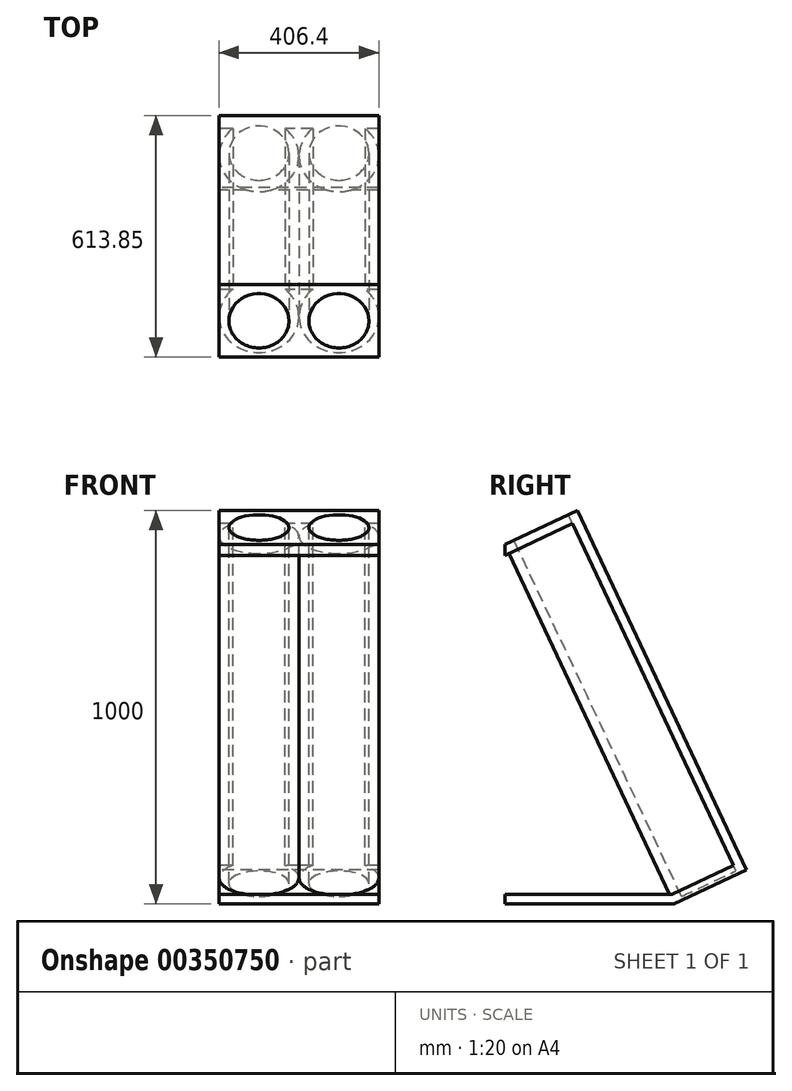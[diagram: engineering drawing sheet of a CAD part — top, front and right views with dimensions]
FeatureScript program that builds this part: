
annotation { "Feature Type Name" : "Feature", "Feature Type Description" : "" }
export const myFeature = defineFeature(function(context is Context, id is Id, definition is map)
    precondition{}
    {
        {
            var Q0;
            Q0=qCreatedBy(makeId("Right.planeOp"),FACE);
            var sketch = newSketch(context, id + "F0", { "sketchPlane" : qUnion([Q0])});
            skLineSegment(sketch, "E0", {"start": v(0, 0) * mm, "end": v(-430, 0) * mm});
            skLineSegment(sketch, "E1", {"start": v(-430, 0) * mm, "end": v(-430, 913.46) * mm});
            skLineSegment(sketch, "E2", {"start": v(-430, 913.46) * mm, "end": v(-246.15, 1000) * mm});
            skLineSegment(sketch, "E3", {"start": v(-430, 913.46) * mm, "end": v(0, 0) * mm});
            skLineSegment(sketch, "E4", {"start": v(0, 0) * mm, "end": v(183.85, 86.54) * mm});
            skLineSegment(sketch, "E5", {"start": v(183.85, 86.54) * mm, "end": v(-246.15, 1000) * mm});
            skLineSegment(sketch, "E6", {"start": v(-246.15, 1000) * mm, "end": v(183.85, 1000) * mm, "construction": true});
            skLineSegment(sketch, "E7", {"start": v(183.85, 1000) * mm, "end": v(183.85, 86.54) * mm, "construction": true});
            skSolve(sketch);
        }
        {
            var Q0;
            Q0=makeQuery(id+"F0.imprint","IMPRINT",FACE,{"disambiguationData":[TD([[makeQuery(id+"F0.imprint","IMPRINT",EDGE,{"derivedFrom":sQuery(id+"F0.wireOp",EDGE,"E2")}),-1.0]])]});
            var Q1;
            Q1=makeQuery(id+"F0.imprint","IMPRINT",FACE,{"disambiguationData":[TD([[makeQuery(id+"F0.imprint","IMPRINT",EDGE,{"derivedFrom":sQuery(id+"F0.wireOp",EDGE,"E0")}),-1.0]])]});
            extrude(context, id + "F1", {"entities" : qUnion([Q0, Q1]), "endBound" : BoundingType.SYMMETRIC, "depth" : (2 * 8 * 25.4) * mm});
        }
        {
            var Q0;
            Q0=makeQuery(id+"F1.opExtrude","SWEPT_FACE",FACE,{"disambiguationData":[OSD([sQuery(id+"F0.wireOp",EDGE,"E2")])]});
            var sketch = newSketch(context, id + "F2", { "sketchPlane" : qUnion([Q0])});
            skCircle(sketch, "E8", {"center": v(-101.6, 101.6) * mm, "radius": 76.2 * mm});
            skCircle(sketch, "E9", {"center": v(101.6, 101.6) * mm, "radius": 76.2 * mm});
            skLineSegment(sketch, "E10", {"start": v(101.6, 203.2) * mm, "end": v(101.6, 177.8) * mm, "construction": true});
            skLineSegment(sketch, "E11", {"start": v(101.6, 25.4) * mm, "end": v(101.6, 0) * mm, "construction": true});
            skLineSegment(sketch, "E12", {"start": v(203.2, 101.6) * mm, "end": v(177.8, 101.6) * mm, "construction": true});
            skLineSegment(sketch, "E13", {"start": v(-101.6, 203.2) * mm, "end": v(-101.6, 177.8) * mm, "construction": true});
            skLineSegment(sketch, "E14", {"start": v(-203.2, 101.6) * mm, "end": v(-177.8, 101.6) * mm, "construction": true});
            skLineSegment(sketch, "E15", {"start": v(-101.6, 0) * mm, "end": v(-101.6, 25.4) * mm, "construction": true});
            skSolve(sketch);
        }
        {
            var Q0;
            Q0=makeQuery(id+"F2.imprint","IMPRINT",FACE,{"disambiguationData":[TD([[makeQuery(id+"F2.imprint","IMPRINT",EDGE,{"derivedFrom":sQuery(id+"F2.wireOp",EDGE,"E8")}),1.0]])]});
            var Q1;
            Q1=makeQuery(id+"F2.imprint","IMPRINT",FACE,{"disambiguationData":[TD([[makeQuery(id+"F2.imprint","IMPRINT",EDGE,{"derivedFrom":sQuery(id+"F2.wireOp",EDGE,"E9")}),1.0]])]});
            extrude(context, id + "F3", {"entities" : qUnion([Q0, Q1]), "operationType" : NewBodyOperationType.REMOVE, "oppositeDirection" : true, "depth" : 1000 * mm});
        }
        {
            var Q0;
            Q0=makeQuery(id+"F1.opExtrude","SWEPT_FACE",FACE,{"disambiguationData":[OSD([sQuery(id+"F0.wireOp",EDGE,"E1")])]});
            var Q1;
            Q1=makeQuery(id+"F1.opExtrude","CAP_FACE",FACE,{"disambiguationData":[OSD([sQuery(id+"F0.wireOp",EDGE,"E0"),sQuery(id+"F0.wireOp",EDGE,"E1"),sQuery(id+"F0.wireOp",EDGE,"E2"),sQuery(id+"F0.wireOp",EDGE,"E4"),sQuery(id+"F0.wireOp",EDGE,"E5")])],"isStart":false});
            var Q2;
            Q2=makeQuery(id+"F1.opExtrude","CAP_FACE",FACE,{"disambiguationData":[OSD([sQuery(id+"F0.wireOp",EDGE,"E0"),sQuery(id+"F0.wireOp",EDGE,"E1"),sQuery(id+"F0.wireOp",EDGE,"E2"),sQuery(id+"F0.wireOp",EDGE,"E4"),sQuery(id+"F0.wireOp",EDGE,"E5")])],"isStart":true});
            shell(context, id + "F4", {"entities" : qUnion([Q0, Q1, Q2]), "thickness" : 25 * mm});
        }
    });
